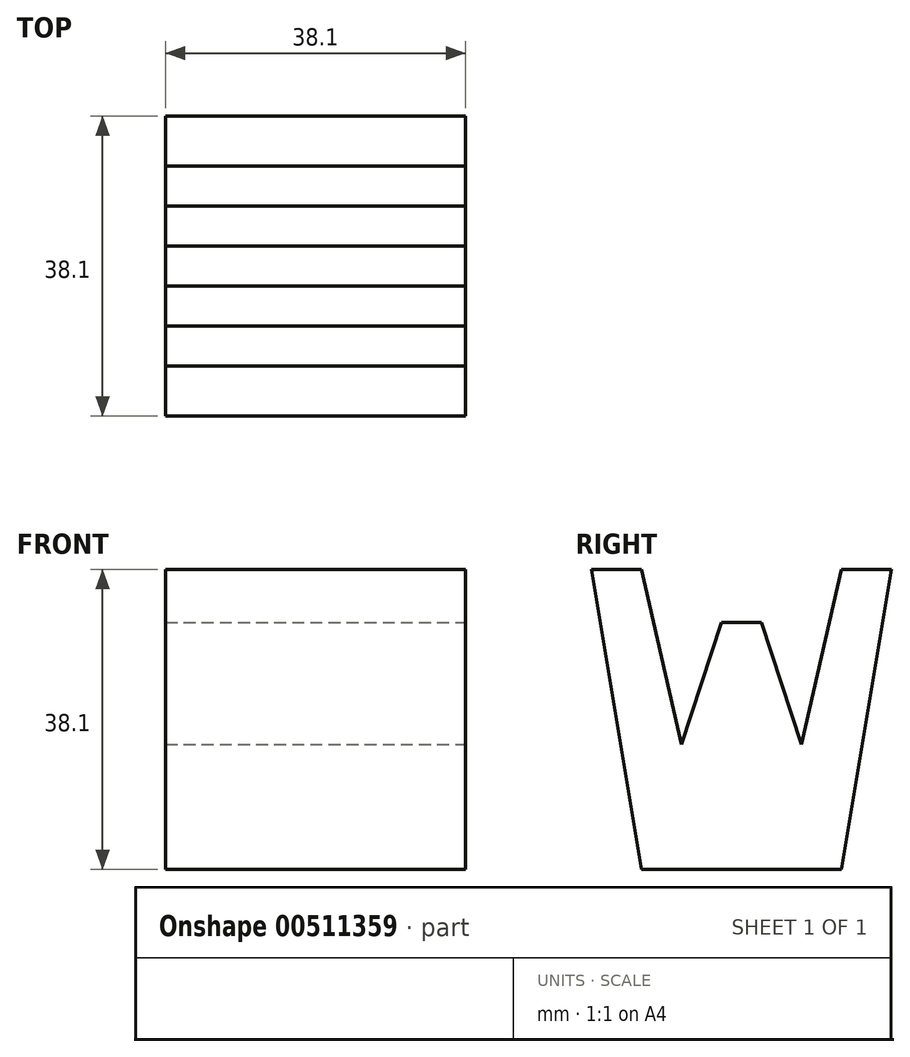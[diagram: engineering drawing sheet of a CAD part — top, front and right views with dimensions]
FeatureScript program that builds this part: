
annotation { "Feature Type Name" : "Feature", "Feature Type Description" : "" }
export const myFeature = defineFeature(function(context is Context, id is Id, definition is map)
    precondition{}
    {
        {
            var Q0;
            Q0=qCreatedBy(makeId("Front.planeOp"),FACE);
            var sketch = newSketch(context, id + "F0", { "sketchPlane" : qUnion([Q0])});
            skLineSegment(sketch, "E0.bottom", {"start": v(0, 0) * mm, "end": v(38.1, 0) * mm});
            skLineSegment(sketch, "E0.top", {"start": v(0, 38.1) * mm, "end": v(38.1, 38.1) * mm});
            skLineSegment(sketch, "E0.left", {"start": v(0, 0) * mm, "end": v(0, 38.1) * mm});
            skLineSegment(sketch, "E0.right", {"start": v(38.1, 0) * mm, "end": v(38.1, 38.1) * mm});
            skSolve(sketch);
        }
        {
            var Q0;
            Q0 = qSketchRegion(id + "F0", true);
            extrude(context, id + "F1", {"entities" : qUnion([Q0]), "depth" : 38.1 * mm, "offsetDistance" : 25.4 * mm});
        }
        {
            var Q0;
            Q0=qCreatedBy(makeId("Front.planeOp"),FACE);
            cPlane(context, id + "F2", {"entities" : qUnion([Q0]), "cplaneType" : CPlaneType.OFFSET, "offset" : 38.1 * mm, "width" : 152.4 * mm, "height" : 152.4 * mm});
        }
        {
            var Q0;
            Q0=qCreatedBy(makeId("Right.planeOp"),FACE);
            cPlane(context, id + "F3", {"entities" : qUnion([Q0]), "cplaneType" : CPlaneType.OFFSET, "offset" : 38.1 * mm, "width" : 152.4 * mm, "height" : 152.4 * mm});
        }
        {
            var Q0;
            Q0=qCreatedBy(id+"F3.planeOp",FACE);
            var sketch = newSketch(context, id + "F4", { "sketchPlane" : qUnion([Q0])});
            skLineSegment(sketch, "E1.bottom", {"start": v(0, 0) * mm, "end": v(-38.1, 0) * mm});
            skLineSegment(sketch, "E1.top", {"start": v(0, 38.1) * mm, "end": v(-38.1, 38.1) * mm});
            skLineSegment(sketch, "E1.left", {"start": v(0, 0) * mm, "end": v(0, 38.1) * mm});
            skLineSegment(sketch, "E1.right", {"start": v(-38.1, 0) * mm, "end": v(-38.1, 38.1) * mm});
            skLineSegment(sketch, "E2", {"start": v(-31.75, 38.1) * mm, "end": v(-26.67, 15.88) * mm});
            skLineSegment(sketch, "E3", {"start": v(-26.67, 15.87) * mm, "end": v(-21.6, 31.36) * mm});
            skLineSegment(sketch, "E4", {"start": v(-21.6, 31.36) * mm, "end": v(-16.51, 31.36) * mm});
            skLineSegment(sketch, "E5", {"start": v(-16.51, 31.36) * mm, "end": v(-11.43, 15.88) * mm});
            skLineSegment(sketch, "E6", {"start": v(-11.43, 15.88) * mm, "end": v(-6.35, 38.1) * mm});
            skLineSegment(sketch, "E7", {"start": v(-11.43, 15.88) * mm, "end": v(-16.51, 31.36) * mm});
            skLineSegment(sketch, "E8", {"start": v(-38.1, 0) * mm, "end": v(-31.75, 0) * mm});
            skLineSegment(sketch, "E9", {"start": v(-38.1, 38.1) * mm, "end": v(-31.75, 0) * mm});
            skLineSegment(sketch, "E10", {"start": v(-25.4, 0) * mm, "end": v(-31.75, 0) * mm});
            skLineSegment(sketch, "E11", {"start": v(-25.4, 0) * mm, "end": v(-19.05, 0) * mm});
            skLineSegment(sketch, "E12", {"start": v(-19.05, 0) * mm, "end": v(-12.7, 0) * mm});
            skPoint(sketch, "E13.start.orphan", {"position": v(-16.51, 0) * mm});
            skLineSegment(sketch, "E14", {"start": v(0, 0) * mm, "end": v(-6.35, 0) * mm});
            skLineSegment(sketch, "E15", {"start": v(-6.35, 0) * mm, "end": v(-12.7, 0) * mm});
            skLineSegment(sketch, "E16", {"start": v(-6.35, 0) * mm, "end": v(0, 38.1) * mm});
            skPoint(sketch, "E17.end.orphan", {"position": v(-17.28, 18.66) * mm});
            skLineSegment(sketch, "E18", {"start": v(-25.4, 0) * mm, "end": v(-19.05, 18.66) * mm});
            skLineSegment(sketch, "E19", {"start": v(-19.05, 18.66) * mm, "end": v(-12.7, 0) * mm});
            skSolve(sketch);
        }
        {
            var Q0;
            Q0=makeQuery(id+"F4.imprint","IMPRINT",FACE,{"disambiguationData":[TD([[makeQuery(id+"F4.imprint","IMPRINT",EDGE,{"derivedFrom":sQuery(id+"F4.wireOp",EDGE,"E1.right")}),-1.0]])]});
            var Q1;
            Q1=makeQuery(id+"F4.imprint","IMPRINT",FACE,{"disambiguationData":[TD([[makeQuery(id+"F4.imprint","IMPRINT",EDGE,{"derivedFrom":sQuery(id+"F4.wireOp",EDGE,"E11")}),1.0]])]});
            var Q2;
            Q2=makeQuery(id+"F4.imprint","IMPRINT",FACE,{"disambiguationData":[TD([[makeQuery(id+"F4.imprint","IMPRINT",EDGE,{"derivedFrom":sQuery(id+"F4.wireOp",EDGE,"E1.left")}),1.0]])]});
            var Q3;
            {var subQ0=sQuery(id+"F4.wireOp",EDGE,"E2");Q3=makeQuery(id+"F4.imprint","IMPRINT",FACE,{"disambiguationData":[TD([[makeQuery(id+"F4.imprint","IMPRINT",EDGE,{"derivedFrom":subQ0}),1.0]])]});}
            extrude(context, id + "F5", {"entities" : qUnion([Q0, Q1, Q2, Q3]), "operationType" : NewBodyOperationType.REMOVE, "oppositeDirection" : true, "depth" : 38.1 * mm, "offsetDistance" : 25.4 * mm});
        }
    });
